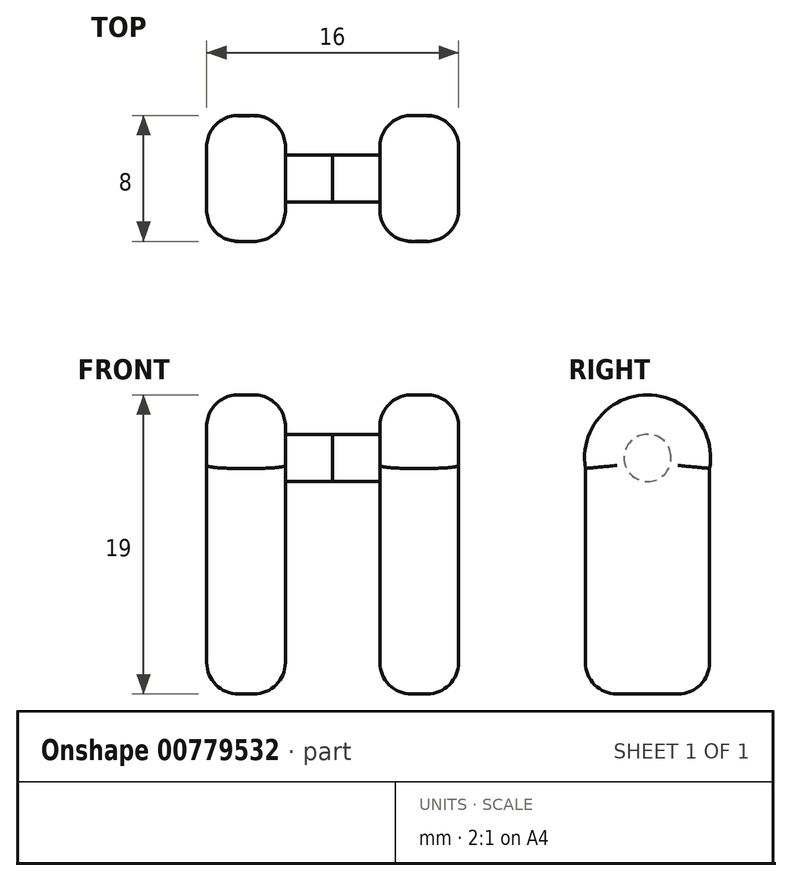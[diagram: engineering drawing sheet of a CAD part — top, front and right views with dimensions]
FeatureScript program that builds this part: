
annotation { "Feature Type Name" : "Feature", "Feature Type Description" : "" }
export const myFeature = defineFeature(function(context is Context, id is Id, definition is map)
    precondition{}
    {
        {
            var Q0;
            Q0=qCreatedBy(makeId("Right.planeOp"),FACE);
            var sketch = newSketch(context, id + "F0", { "sketchPlane" : qUnion([Q0])});
            skCircle(sketch, "E0", {"center": v(0, 0) * mm, "radius": 1.5 * mm});
            skSolve(sketch);
        }
        {
            var Q0;
            Q0 = qSketchRegion(id + "F0", true);
            extrude(context, id + "F1", {"entities" : qUnion([Q0]), "depth" : 3 * mm, "offsetDistance" : 25 * mm});
        }
        {
            var Q0;
            Q0=qCreatedBy(makeId("Right.planeOp"),FACE);
            var sketch = newSketch(context, id + "F2", { "sketchPlane" : qUnion([Q0])});
            skCircle(sketch, "E1", {"center": v(0, 0) * mm, "radius": 4 * mm});
            skSolve(sketch);
        }
        {
            var Q0;
            Q0=qCreatedBy(makeId("Right.planeOp"),FACE);
            var sketch = newSketch(context, id + "F3", { "sketchPlane" : qUnion([Q0])});
            skLineSegment(sketch, "E2.bottom", {"start": v(3.94, 0) * mm, "end": v(-3.94, 0) * mm});
            skLineSegment(sketch, "E2.top", {"start": v(3.94, -15) * mm, "end": v(-3.94, -15) * mm});
            skLineSegment(sketch, "E2.left", {"start": v(3.94, 0) * mm, "end": v(3.94, -15) * mm});
            skLineSegment(sketch, "E2.right", {"start": v(-3.94, 0) * mm, "end": v(-3.94, -15) * mm});
            skPoint(sketch, "E2.middle", {"position": v(0, -7.5) * mm});
            skSolve(sketch);
        }
        {
            var Q0;
            Q0=makeQuery(id+"F2.imprint","IMPRINT",FACE,{"disambiguationData":[TD([[makeQuery(id+"F2.imprint","IMPRINT",EDGE,{"derivedFrom":sQuery(id+"F2.wireOp",EDGE,"E1")}),1.0]])]});
            var Q1;
            Q1=makeQuery(id+"F3.imprint","IMPRINT",FACE,{"disambiguationData":[TD([[makeQuery(id+"F3.imprint","IMPRINT",EDGE,{"derivedFrom":sQuery(id+"F3.wireOp",EDGE,"E2.bottom")}),1.0]])]});
            extrude(context, id + "F4", {"entities" : qUnion([Q0, Q1]), "operationType" : NewBodyOperationType.ADD, "oppositeDirection" : true, "depth" : 5 * mm, "offsetDistance" : 25 * mm});
        }
        {
            var Q0;
            Q0=makeQuery(id+"F4.opExtrude","CAP_EDGE",EDGE,{"disambiguationData":[OSD([sQuery(id+"F3.wireOp",EDGE,"E2.right")])],"isStart":false});
            var Q1;
            Q1=makeQuery(id+"F4.opExtrude","CAP_EDGE",EDGE,{"disambiguationData":[OSD([sQuery(id+"F3.wireOp",EDGE,"E2.right")])],"isStart":true});
            var Q2;
            Q2=makeQuery(id+"F4.opExtrude","CAP_EDGE",EDGE,{"disambiguationData":[OSD([sQuery(id+"F3.wireOp",EDGE,"E2.left")])],"isStart":true});
            var Q3;
            Q3=makeQuery(id+"F4.opExtrude","CAP_EDGE",EDGE,{"disambiguationData":[OSD([sQuery(id+"F3.wireOp",EDGE,"E2.left")])],"isStart":false});
            var Q4;
            Q4=makeQuery(id+"F4.opExtrude","SWEPT_EDGE",EDGE,{"disambiguationData":[OSD([sQuery(id+"F3.wireOp",EDGE,"E2.top"),sQuery(id+"F3.wireOp",EDGE,"E2.left")])]});
            var Q5;
            Q5=makeQuery(id+"F4.opExtrude","CAP_EDGE",EDGE,{"disambiguationData":[OSD([sQuery(id+"F3.wireOp",EDGE,"E2.top")])],"isStart":false});
            var Q6;
            Q6=makeQuery(id+"F4.opExtrude","SWEPT_EDGE",EDGE,{"disambiguationData":[OSD([sQuery(id+"F3.wireOp",EDGE,"E2.top"),sQuery(id+"F3.wireOp",EDGE,"E2.right")])]});
            var Q7;
            Q7=makeQuery(id+"F4.opExtrude","CAP_EDGE",EDGE,{"disambiguationData":[OSD([sQuery(id+"F3.wireOp",EDGE,"E2.top")])],"isStart":true});
            fillet(context, id + "F5", {"entities" : qUnion([Q0, Q1, Q2, Q3, Q4, Q5, Q6, Q7]), "radius" : 2 * mm, "tangentPropagation" : true, "allowEdgeOverflow" : false});
        }
        {
            var Q0;
            Q0=makeQuery(id+"F4.opExtrude","CAP_EDGE",EDGE,{"disambiguationData":[OSD([sQuery(id+"F2.wireOp",EDGE,"E1")])],"isStart":false});
            var Q1;
            Q1=makeQuery(id+"F4.opExtrude","CAP_EDGE",EDGE,{"disambiguationData":[OSD([sQuery(id+"F2.wireOp",EDGE,"E1")])],"isStart":true});
            fillet(context, id + "F6", {"entities" : qUnion([Q0, Q1]), "radius" : 2 * mm, "tangentPropagation" : true, "allowEdgeOverflow" : false});
        }
        {
            var Q0;
            Q0=makeQuery(id+"F1.opExtrude","SWEPT_BODY",BODY,{"disambiguationData":[OSD([sQuery(id+"F0.wireOp",EDGE,"E0")])]});
            var Q1;
            Q1=makeQuery(id+"F1.opExtrude","CAP_FACE",FACE,{"disambiguationData":[OSD([sQuery(id+"F0.wireOp",EDGE,"E0")])],"isStart":false});
            mirror(context, id + "F7", {"entities" : qUnion([Q0]), "mirrorPlane" : qUnion([Q1])});
        }
    });
